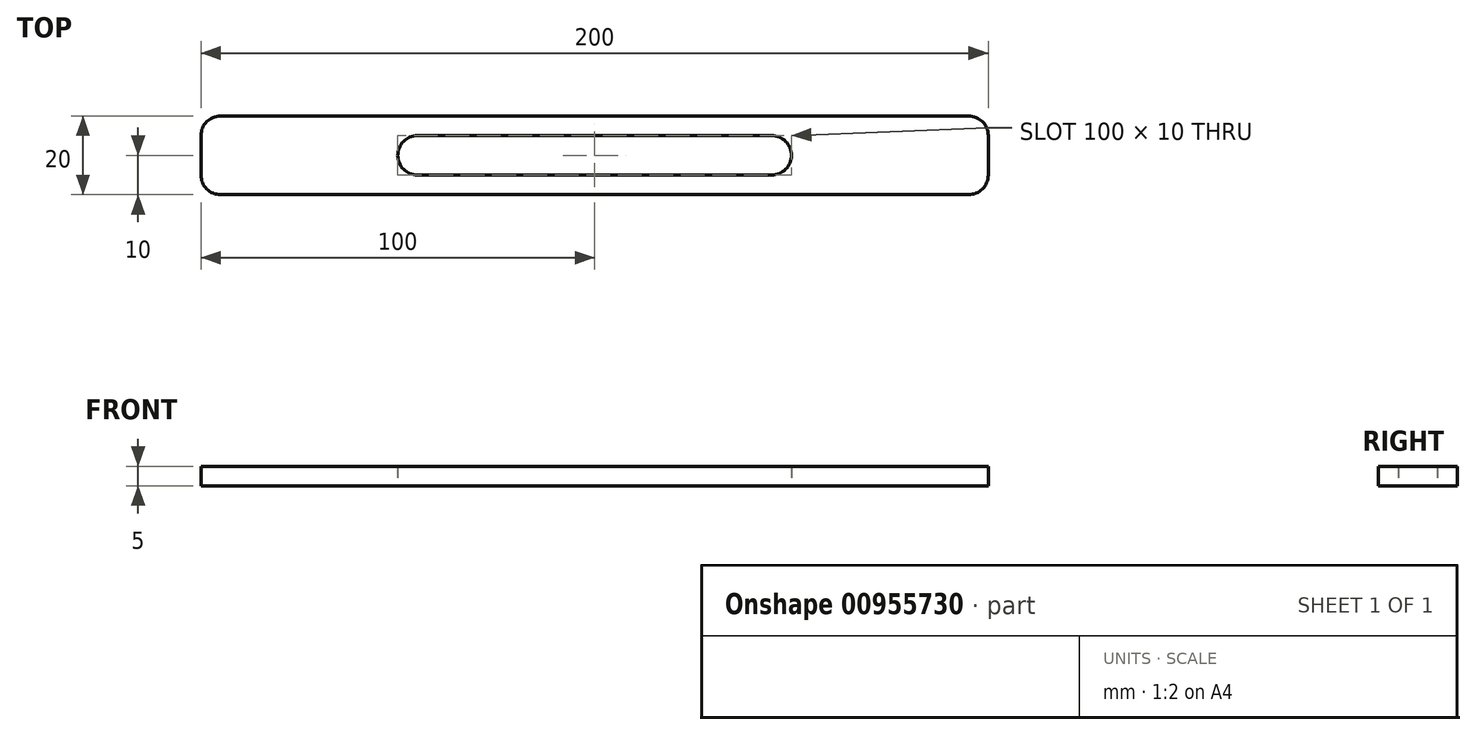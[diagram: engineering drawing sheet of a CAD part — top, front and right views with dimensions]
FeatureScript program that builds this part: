
annotation { "Feature Type Name" : "Feature", "Feature Type Description" : "" }
export const myFeature = defineFeature(function(context is Context, id is Id, definition is map)
    precondition{}
    {
        {
            var Q0;
            Q0=qCreatedBy(makeId("Top.planeOp"),FACE);
            var sketch = newSketch(context, id + "F0", { "sketchPlane" : qUnion([Q0])});
            skLineSegment(sketch, "E0.bottom", {"start": v(100, 10) * mm, "end": v(-100, 10) * mm});
            skLineSegment(sketch, "E0.top", {"start": v(100, -10) * mm, "end": v(-100, -10) * mm});
            skLineSegment(sketch, "E0.left", {"start": v(100, 10) * mm, "end": v(100, -10) * mm});
            skLineSegment(sketch, "E0.right", {"start": v(-100, 10) * mm, "end": v(-100, -10) * mm});
            skPoint(sketch, "E0.middle", {"position": v(0, 0) * mm});
            skLineSegment(sketch, "E1.bottom", {"start": v(45, -5) * mm, "end": v(-45, -5) * mm});
            skLineSegment(sketch, "E1.top", {"start": v(45, 5) * mm, "end": v(-45, 5) * mm});
            skLineSegment(sketch, "E1.left", {"start": v(50, 0) * mm, "end": v(50, 0) * mm});
            skLineSegment(sketch, "E1.right", {"start": v(-50, 0) * mm, "end": v(-50, 0) * mm});
            skPoint(sketch, "E2.visualSharp", {"position": v(-50, 5) * mm});
            skArc(sketch, "E2.filletArc", {"start": v(-45, 5) * mm, "mid": v(-48.54, 3.54) * mm, "end": v(-50, 0) * mm});
            skPoint(sketch, "E3.visualSharp", {"position": v(-50, -5) * mm});
            skArc(sketch, "E3.filletArc", {"start": v(-50, 0) * mm, "mid": v(-48.54, -3.54) * mm, "end": v(-45, -5) * mm});
            skPoint(sketch, "E4.visualSharp", {"position": v(50, 5) * mm});
            skArc(sketch, "E4.filletArc", {"start": v(50, 0) * mm, "mid": v(48.54, 3.54) * mm, "end": v(45, 5) * mm});
            skPoint(sketch, "E5.visualSharp", {"position": v(50, -5) * mm});
            skArc(sketch, "E5.filletArc", {"start": v(45, -5) * mm, "mid": v(48.54, -3.54) * mm, "end": v(50, 0) * mm});
            skSolve(sketch);
        }
        {
            var Q0;
            Q0=makeQuery(id+"F0.imprint","IMPRINT",FACE,{"disambiguationData":[TD([[makeQuery(id+"F0.imprint","IMPRINT",EDGE,{"derivedFrom":sQuery(id+"F0.wireOp",EDGE,"E0.bottom")}),1.0]])]});
            extrude(context, id + "F1", {"entities" : qUnion([Q0]), "depth" : 5 * mm, "offsetDistance" : 25 * mm});
        }
        {
            var Q0;
            Q0=makeQuery(id+"F1.opExtrude","SWEPT_EDGE",EDGE,{"disambiguationData":[OSD([sQuery(id+"F0.wireOp",EDGE,"E0.top"),sQuery(id+"F0.wireOp",EDGE,"E0.right")])]});
            var Q1;
            Q1=makeQuery(id+"F1.opExtrude","SWEPT_EDGE",EDGE,{"disambiguationData":[OSD([sQuery(id+"F0.wireOp",EDGE,"E0.top"),sQuery(id+"F0.wireOp",EDGE,"E0.left")])]});
            var Q2;
            Q2=makeQuery(id+"F1.opExtrude","SWEPT_EDGE",EDGE,{"disambiguationData":[OSD([sQuery(id+"F0.wireOp",EDGE,"E0.bottom"),sQuery(id+"F0.wireOp",EDGE,"E0.left")])]});
            var Q3;
            Q3=makeQuery(id+"F1.opExtrude","SWEPT_EDGE",EDGE,{"disambiguationData":[OSD([sQuery(id+"F0.wireOp",EDGE,"E0.bottom"),sQuery(id+"F0.wireOp",EDGE,"E0.right")])]});
            fillet(context, id + "F2", {"entities" : qUnion([Q0, Q1, Q2, Q3]), "radius" : 5 * mm, "tangentPropagation" : true, "allowEdgeOverflow" : false});
        }
    });
